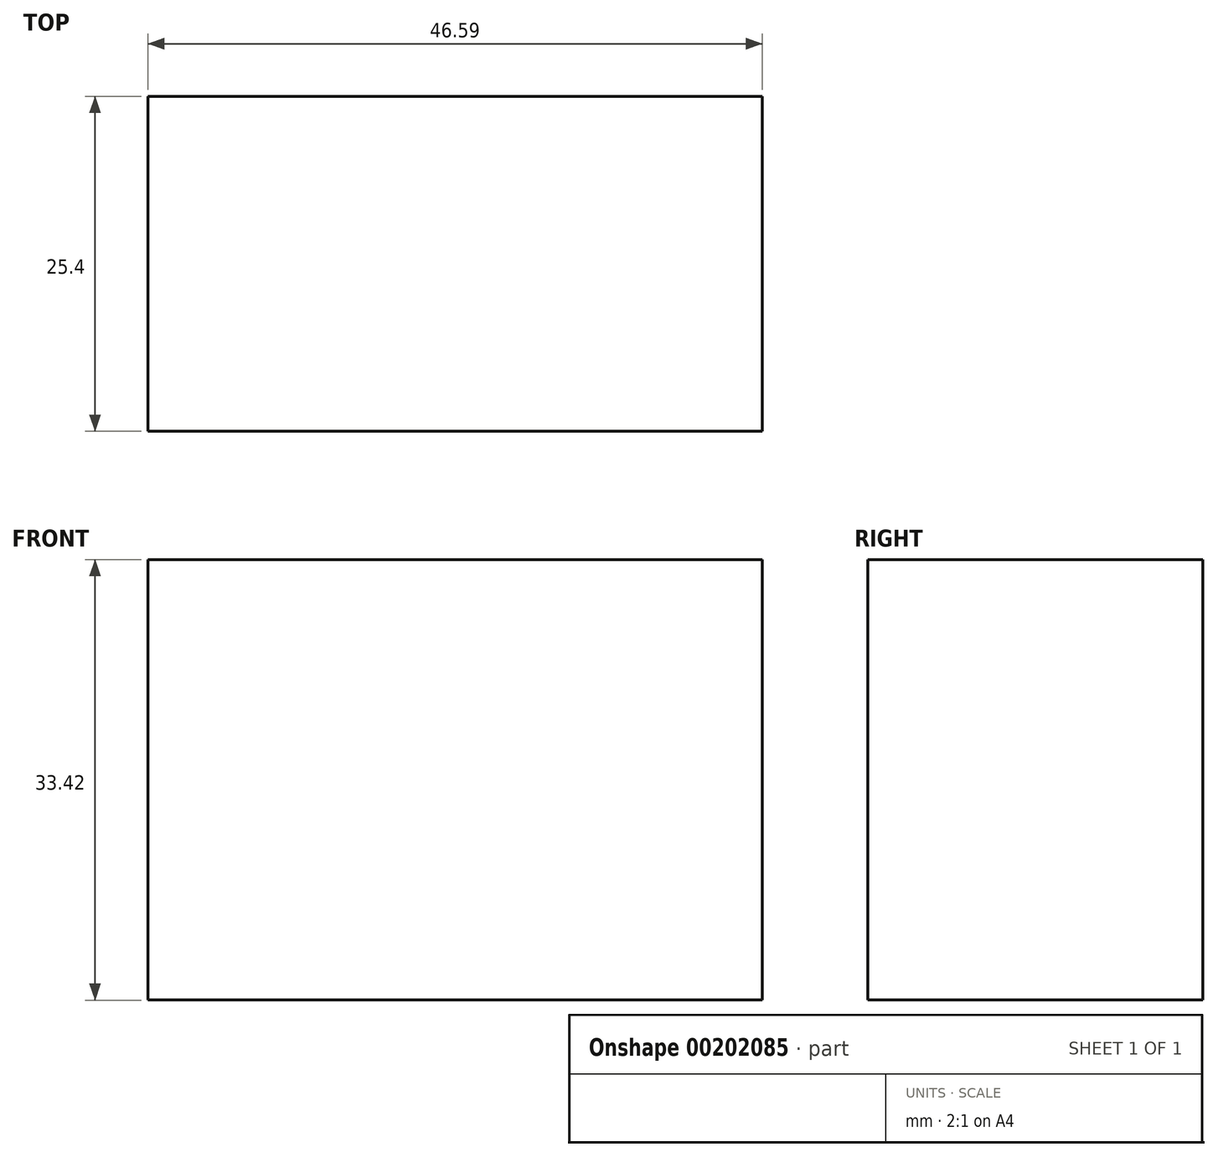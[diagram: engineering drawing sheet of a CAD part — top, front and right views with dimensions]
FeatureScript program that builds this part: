
annotation { "Feature Type Name" : "Feature", "Feature Type Description" : "" }
export const myFeature = defineFeature(function(context is Context, id is Id, definition is map)
    precondition{}
    {
        {
            var Q0;
            Q0=qCreatedBy(makeId("Front.planeOp"),FACE);
            var sketch = newSketch(context, id + "F0", { "sketchPlane" : qUnion([Q0])});
            skLineSegment(sketch, "E0.bottom", {"start": v(-71.14, 28.55) * mm, "end": v(-24.55, 28.55) * mm});
            skLineSegment(sketch, "E0.top", {"start": v(-71.14, 61.97) * mm, "end": v(-24.55, 61.97) * mm});
            skLineSegment(sketch, "E0.left", {"start": v(-71.14, 28.55) * mm, "end": v(-71.14, 61.97) * mm});
            skLineSegment(sketch, "E0.right", {"start": v(-24.55, 28.55) * mm, "end": v(-24.55, 61.97) * mm});
            skSolve(sketch);
        }
        {
            var Q0;
            Q0=makeQuery(id+"F0.imprint","IMPRINT",FACE,{"disambiguationData":[TD([[makeQuery(id+"F0.imprint","IMPRINT",EDGE,{"derivedFrom":sQuery(id+"F0.wireOp",EDGE,"E0.bottom")}),1.0]])]});
            extrude(context, id + "F1", {"entities" : qUnion([Q0]), "depth" : 25.4 * mm});
        }
    });
